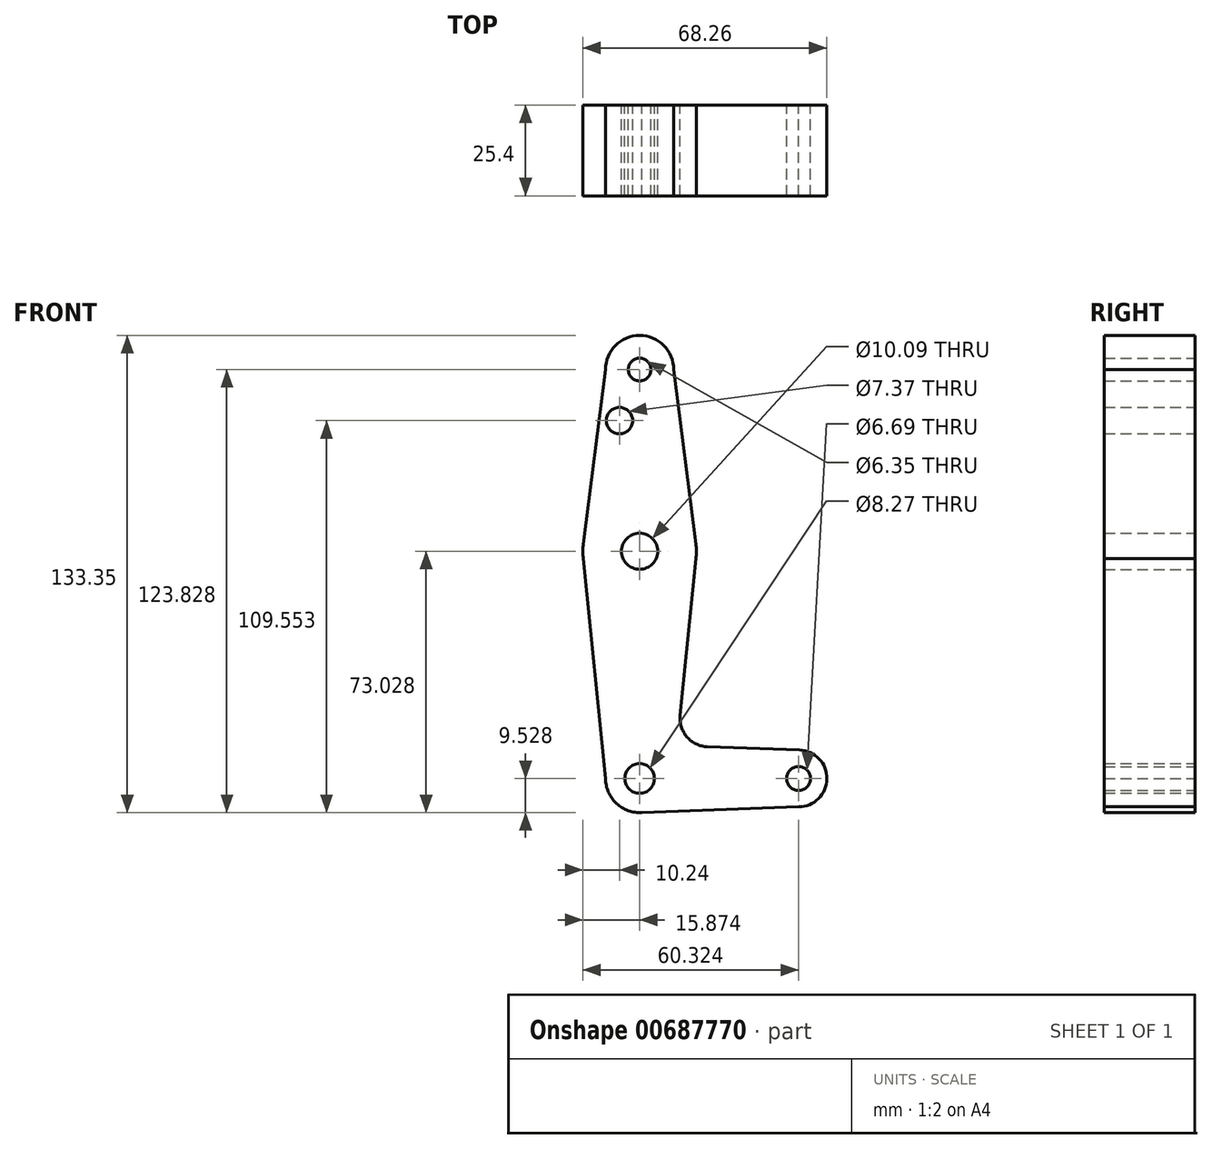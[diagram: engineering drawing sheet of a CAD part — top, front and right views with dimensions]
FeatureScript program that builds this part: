
annotation { "Feature Type Name" : "Feature", "Feature Type Description" : "" }
export const myFeature = defineFeature(function(context is Context, id is Id, definition is map)
    precondition{}
    {
        {
            var Q0;
            Q0=qCreatedBy(makeId("Front.planeOp"),FACE);
            var sketch = newSketch(context, id + "F0", { "sketchPlane" : qUnion([Q0])});
            skLineSegment(sketch, "E0", {"start": v(-42.93, 60) * mm, "end": v(-42.93, -54.3) * mm, "construction": true});
            skLineSegment(sketch, "E1", {"start": v(-42.93, -54.3) * mm, "end": v(1.52, -54.3) * mm, "construction": true});
            skCircle(sketch, "E2", {"center": v(-42.93, 60) * mm, "radius": 9.53 * mm});
            skCircle(sketch, "E3", {"center": v(-42.93, 9.2) * mm, "radius": 15.88 * mm});
            skCircle(sketch, "E4", {"center": v(-42.93, -54.3) * mm, "radius": 9.53 * mm});
            skCircle(sketch, "E5", {"center": v(1.52, -54.3) * mm, "radius": 7.94 * mm});
            skLineSegment(sketch, "E6", {"start": v(-52.45, 60) * mm, "end": v(-58.67, 11.22) * mm});
            skLineSegment(sketch, "E7", {"start": v(-58.67, 7.2) * mm, "end": v(-52.45, -54.3) * mm});
            skLineSegment(sketch, "E8", {"start": v(-33.4, 60) * mm, "end": v(-27.18, 11.22) * mm});
            skLineSegment(sketch, "E9", {"start": v(-27.18, 7.2) * mm, "end": v(-31.59, -36.7) * mm});
            skLineSegment(sketch, "E10", {"start": v(-23.96, -45.44) * mm, "end": v(1.8, -46.36) * mm});
            skLineSegment(sketch, "E11", {"start": v(-42.93, -63.82) * mm, "end": v(1.52, -62.23) * mm});
            skCircle(sketch, "E12", {"center": v(-42.93, 9.2) * mm, "radius": 5.05 * mm});
            skCircle(sketch, "E13", {"center": v(-48.56, 45.73) * mm, "radius": 3.69 * mm});
            skCircle(sketch, "E14", {"center": v(-42.93, -54.3) * mm, "radius": 4.14 * mm});
            skCircle(sketch, "E15", {"center": v(1.52, -54.3) * mm, "radius": 3.34 * mm});
            skCircle(sketch, "E16", {"center": v(-42.93, 60) * mm, "radius": 3.18 * mm});
            skArc(sketch, "E17.filletArc", {"start": v(-31.59, -36.7) * mm, "mid": v(-29.67, -42.72) * mm, "end": v(-23.96, -45.44) * mm});
            skSolve(sketch);
        }
        {
            var Q0;
            Q0 = qSketchRegion(id + "F0", true);
            extrude(context, id + "F1", {"entities" : qUnion([Q0]), "depth" : 25.4 * mm, "offsetDistance" : 25.4 * mm});
        }
    });
